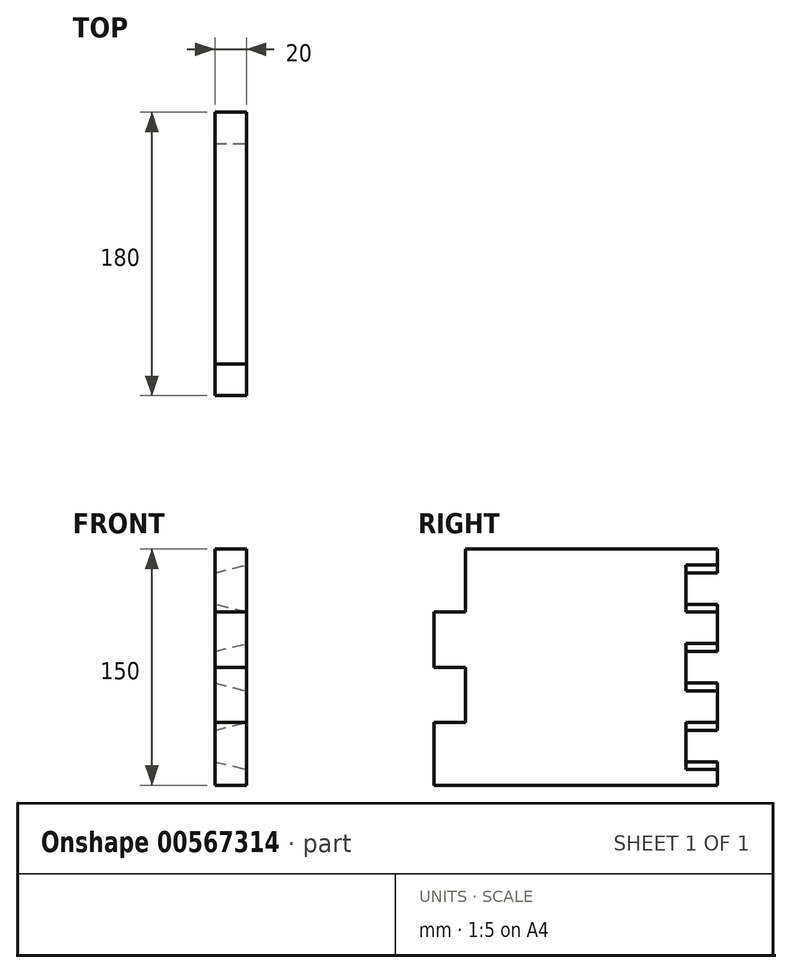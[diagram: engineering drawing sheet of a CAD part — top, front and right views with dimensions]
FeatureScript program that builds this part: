
annotation { "Feature Type Name" : "Feature", "Feature Type Description" : "" }
export const myFeature = defineFeature(function(context is Context, id is Id, definition is map)
    precondition{}
    {
        {
            var Q0;
            Q0=qCreatedBy(makeId("Right.planeOp"),FACE);
            var sketch = newSketch(context, id + "F0", { "sketchPlane" : qUnion([Q0])});
            skLineSegment(sketch, "E0.bottom", {"start": v(-103.5, 91.6) * mm, "end": v(56.5, 91.6) * mm});
            skLineSegment(sketch, "E0.top", {"start": v(-123.5, -58.4) * mm, "end": v(56.5, -58.4) * mm});
            skLineSegment(sketch, "E0.left", {"start": v(-123.5, 51.6) * mm, "end": v(-123.5, 16.6) * mm});
            skLineSegment(sketch, "E0.right", {"start": v(56.5, 91.6) * mm, "end": v(56.5, -58.4) * mm});
            skLineSegment(sketch, "E1", {"start": v(-103.5, 91.6) * mm, "end": v(-103.5, -58.4) * mm});
            skLineSegment(sketch, "E2", {"start": v(-123.5, 16.6) * mm, "end": v(-103.5, 16.6) * mm});
            skLineSegment(sketch, "E3", {"start": v(-123.5, 51.6) * mm, "end": v(-103.5, 51.6) * mm});
            skLineSegment(sketch, "E4", {"start": v(-123.5, -18.4) * mm, "end": v(-103.5, -18.4) * mm});
            skPoint(sketch, "E5.orphan", {"position": v(-123.5, 91.6) * mm});
            skLineSegment(sketch, "E6.trimOffspring", {"start": v(-123.5, -18.4) * mm, "end": v(-123.5, -58.4) * mm});
            skLineSegment(sketch, "E7", {"start": v(36.5, 91.6) * mm, "end": v(36.5, -58.4) * mm});
            skSolve(sketch);
        }
        {
            var Q0;
            Q0 = qSketchRegion(id + "F0", true);
            extrude(context, id + "F1", {"entities" : qUnion([Q0]), "depth" : 20 * mm, "offsetDistance" : 25 * mm});
        }
        {
            var Q0;
            Q0=makeQuery(id+"F1.opExtrude","SWEPT_FACE",FACE,{"disambiguationData":[OSD([sQuery(id+"F0.wireOp",EDGE,"E0.right")])]});
            var sketch = newSketch(context, id + "F2", { "sketchPlane" : qUnion([Q0])});
            skLineSegment(sketch, "E8", {"start": v(0, 26.6) * mm, "end": v(-20, 31.6) * mm});
            skLineSegment(sketch, "E9", {"start": v(0, 6.6) * mm, "end": v(-20, 1.6) * mm});
            skLineSegment(sketch, "E10", {"start": v(-20, 51.6) * mm, "end": v(0, 56.6) * mm});
            skLineSegment(sketch, "E11", {"start": v(0, 76.6) * mm, "end": v(-20, 81.6) * mm});
            skLineSegment(sketch, "E12", {"start": v(0, -23.4) * mm, "end": v(-20, -18.4) * mm});
            skLineSegment(sketch, "E13", {"start": v(0, -43.4) * mm, "end": v(-20, -48.4) * mm});
            skSolve(sketch);
        }
        {
            var Q0;
            {var subQ0=sQuery(id+"F2.wireOp",EDGE,"E10");Q0=makeQuery(id+"F2.imprint","IMPRINT",FACE,{"disambiguationData":[TD([[makeQuery(id+"F2.imprint","IMPRINT",EDGE,{"derivedFrom":subQ0}),1.0]])]});}
            var Q1;
            {var subQ0=sQuery(id+"F2.wireOp",EDGE,"E8");Q1=makeQuery(id+"F2.imprint","IMPRINT",FACE,{"disambiguationData":[TD([[makeQuery(id+"F2.imprint","IMPRINT",EDGE,{"derivedFrom":subQ0}),1.0]])]});}
            var Q2;
            {var subQ0=sQuery(id+"F2.wireOp",EDGE,"E12");Q2=makeQuery(id+"F2.imprint","IMPRINT",FACE,{"disambiguationData":[TD([[makeQuery(id+"F2.imprint","IMPRINT",EDGE,{"derivedFrom":subQ0}),1.0]])]});}
            extrude(context, id + "F3", {"entities" : qUnion([Q0, Q1, Q2]), "operationType" : NewBodyOperationType.REMOVE, "oppositeDirection" : true, "depth" : 20 * mm, "offsetDistance" : 25 * mm});
        }
    });
